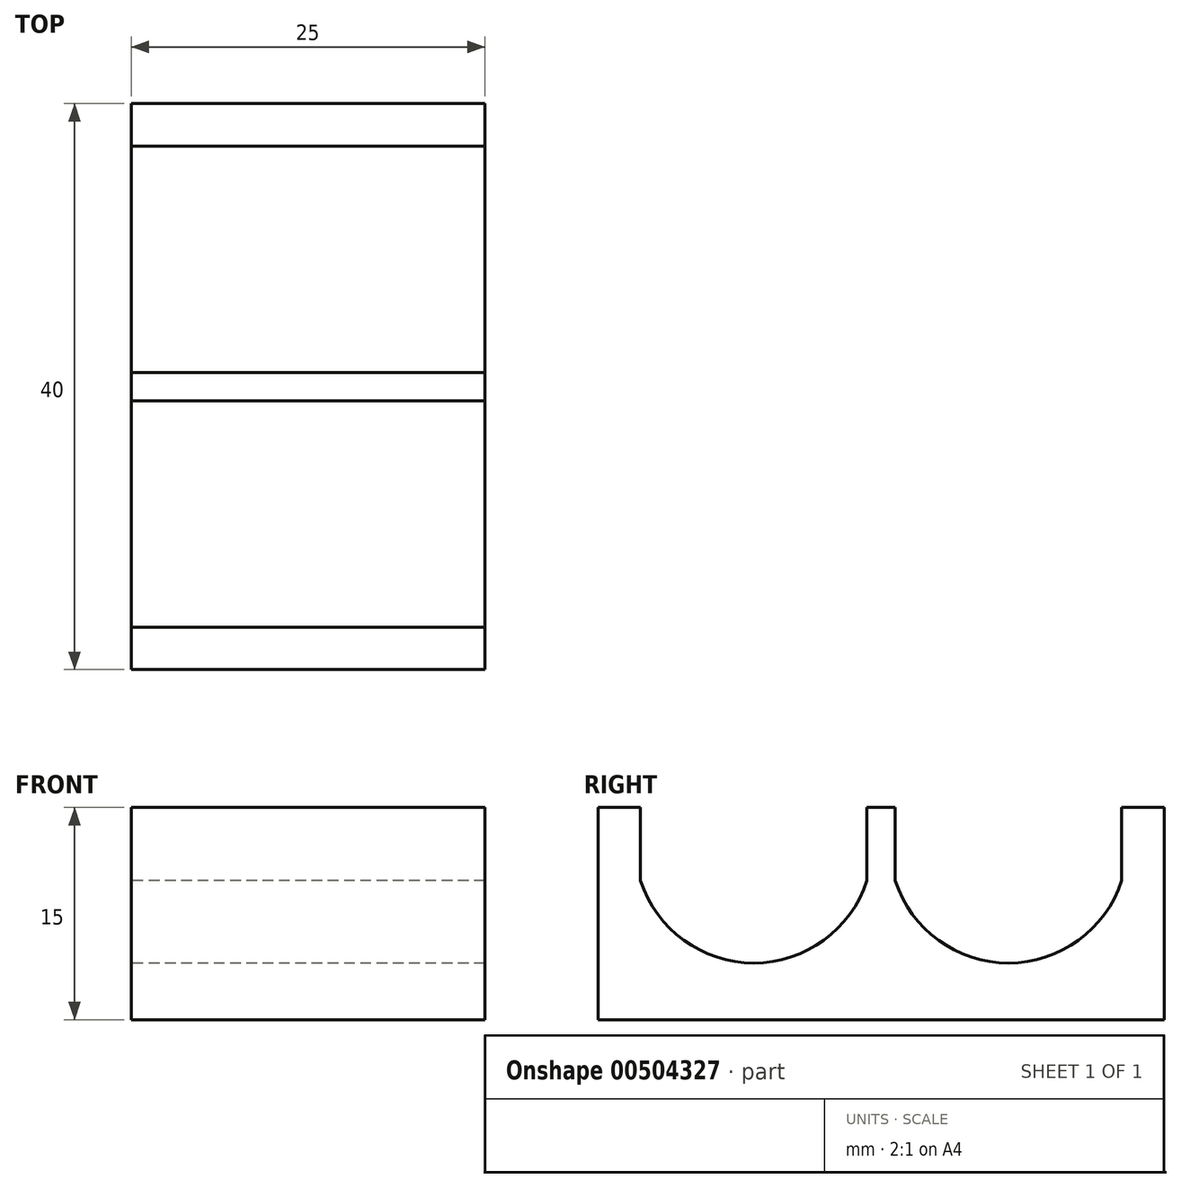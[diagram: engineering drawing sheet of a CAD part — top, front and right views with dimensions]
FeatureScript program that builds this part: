
annotation { "Feature Type Name" : "Feature", "Feature Type Description" : "" }
export const myFeature = defineFeature(function(context is Context, id is Id, definition is map)
    precondition{}
    {
        {
            var Q0;
            Q0=qCreatedBy(makeId("Right.planeOp"),FACE);
            var sketch = newSketch(context, id + "F0", { "sketchPlane" : qUnion([Q0])});
            skLineSegment(sketch, "E0.bottom", {"start": v(20, -7.5) * mm, "end": v(-20, -7.5) * mm});
            skLineSegment(sketch, "E0.top", {"start": v(20, 7.5) * mm, "end": v(-20, 7.5) * mm});
            skLineSegment(sketch, "E0.left", {"start": v(20, -7.5) * mm, "end": v(20, 7.5) * mm});
            skLineSegment(sketch, "E0.right", {"start": v(-20, -7.5) * mm, "end": v(-20, 7.5) * mm});
            skPoint(sketch, "E0.middle", {"position": v(0, 0) * mm});
            skLineSegment(sketch, "E1", {"start": v(-20, 7.5) * mm, "end": v(-17, 7.5) * mm});
            skLineSegment(sketch, "E2", {"start": v(20, 7.5) * mm, "end": v(17, 7.5) * mm});
            skLineSegment(sketch, "E3", {"start": v(-17, 7.5) * mm, "end": v(-1, 7.5) * mm});
            skLineSegment(sketch, "E4", {"start": v(17, 7.5) * mm, "end": v(1, 7.5) * mm});
            skLineSegment(sketch, "E5", {"start": v(1, 7.5) * mm, "end": v(-1, 7.5) * mm});
            skLineSegment(sketch, "E6", {"start": v(-17, 7.5) * mm, "end": v(-17, 2.32) * mm});
            skLineSegment(sketch, "E7", {"start": v(17, 7.5) * mm, "end": v(17, 2.32) * mm});
            skArc(sketch, "E8", {"start": v(-17, 2.32) * mm, "mid": v(-9, -3.5) * mm, "end": v(-1, 2.32) * mm});
            skArc(sketch, "E9", {"start": v(1, 2.32) * mm, "mid": v(9, -3.5) * mm, "end": v(17, 2.32) * mm});
            skLineSegment(sketch, "E10", {"start": v(-1, 7.5) * mm, "end": v(-1, 2.32) * mm});
            skLineSegment(sketch, "E11", {"start": v(1, 7.5) * mm, "end": v(1, 2.32) * mm});
            skSolve(sketch);
        }
        {
            var Q0;
            Q0=makeQuery(id+"F0.imprint","IMPRINT",FACE,{"disambiguationData":[TD([[makeQuery(id+"F0.imprint","IMPRINT",EDGE,{"derivedFrom":sQuery(id+"F0.wireOp",EDGE,"E0.bottom")}),-1.0]])]});
            extrude(context, id + "F1", {"entities" : qUnion([Q0]), "depth" : 25 * mm});
        }
    });
